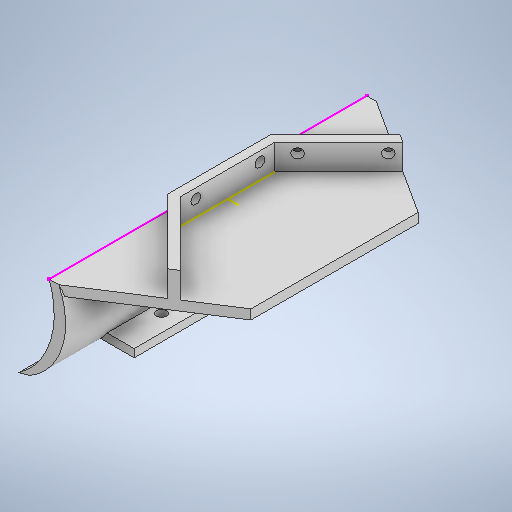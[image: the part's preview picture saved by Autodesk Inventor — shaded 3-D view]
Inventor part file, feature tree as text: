
AUTODESK INVENTOR PART (.ipt)
format: ipt  version: 2025.1 (Build 291241020, 241B)  size: 321,536 bytes
history: native  units: in
note: dims shown in document units (in); Inventor stores cm internally (conversion verified against a paired STEP export)
features: other x3, sketch x3, extrude x2
ambient origin geometry x8: Origin, YZ Plane, XZ Plane, XY Plane, X Axis, Y Axis, Z Axis, Center Point
bodies: Solid1 (feature_tree)
feature tree (8):
  other  "slopeAssembly.iam"
  other  "slope.ipt:1"
  other  "distanceSensorMountIncl.ipt:1"
  extrude  "Extrusion1"  Depth=0.3937in TaperAngle=0.0deg
  extrude  "Extrusion2"  Depth=0.3937in TaperAngle=0.0deg
  sketch  "Sketch12_1"  dims[d0=0.3937in d1=1.0in d2=0.0in]
  sketch  "Sketch3"  dims[d3=0.3937in d4=1.0in d5=0.0in]
  sketch  "Sketch4"
